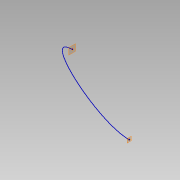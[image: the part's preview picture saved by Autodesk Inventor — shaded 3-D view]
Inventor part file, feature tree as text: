
AUTODESK INVENTOR PART (.ipt)
format: ipt  version: 2019 (Build 230136000, 136)  size: 87,040 bytes
history: native  units: mm
features: other x2, plane x2, sketch x1
ambient origin geometry x8: Origin, YZ Plane, XZ Plane, XY Plane, X Axis, Y Axis, Z Axis, Center Point
feature tree (5):
  other  "Punto de trabajo1"
  other  "Punto de trabajo2"
  plane  "Plano de trabajo1"
  plane  "Plano de trabajo2"
  sketch  "Boceto 3D1"  dims[d0=-10.0mm d1=-0.1mm d2=10.0mm d3=-0.1mm]
